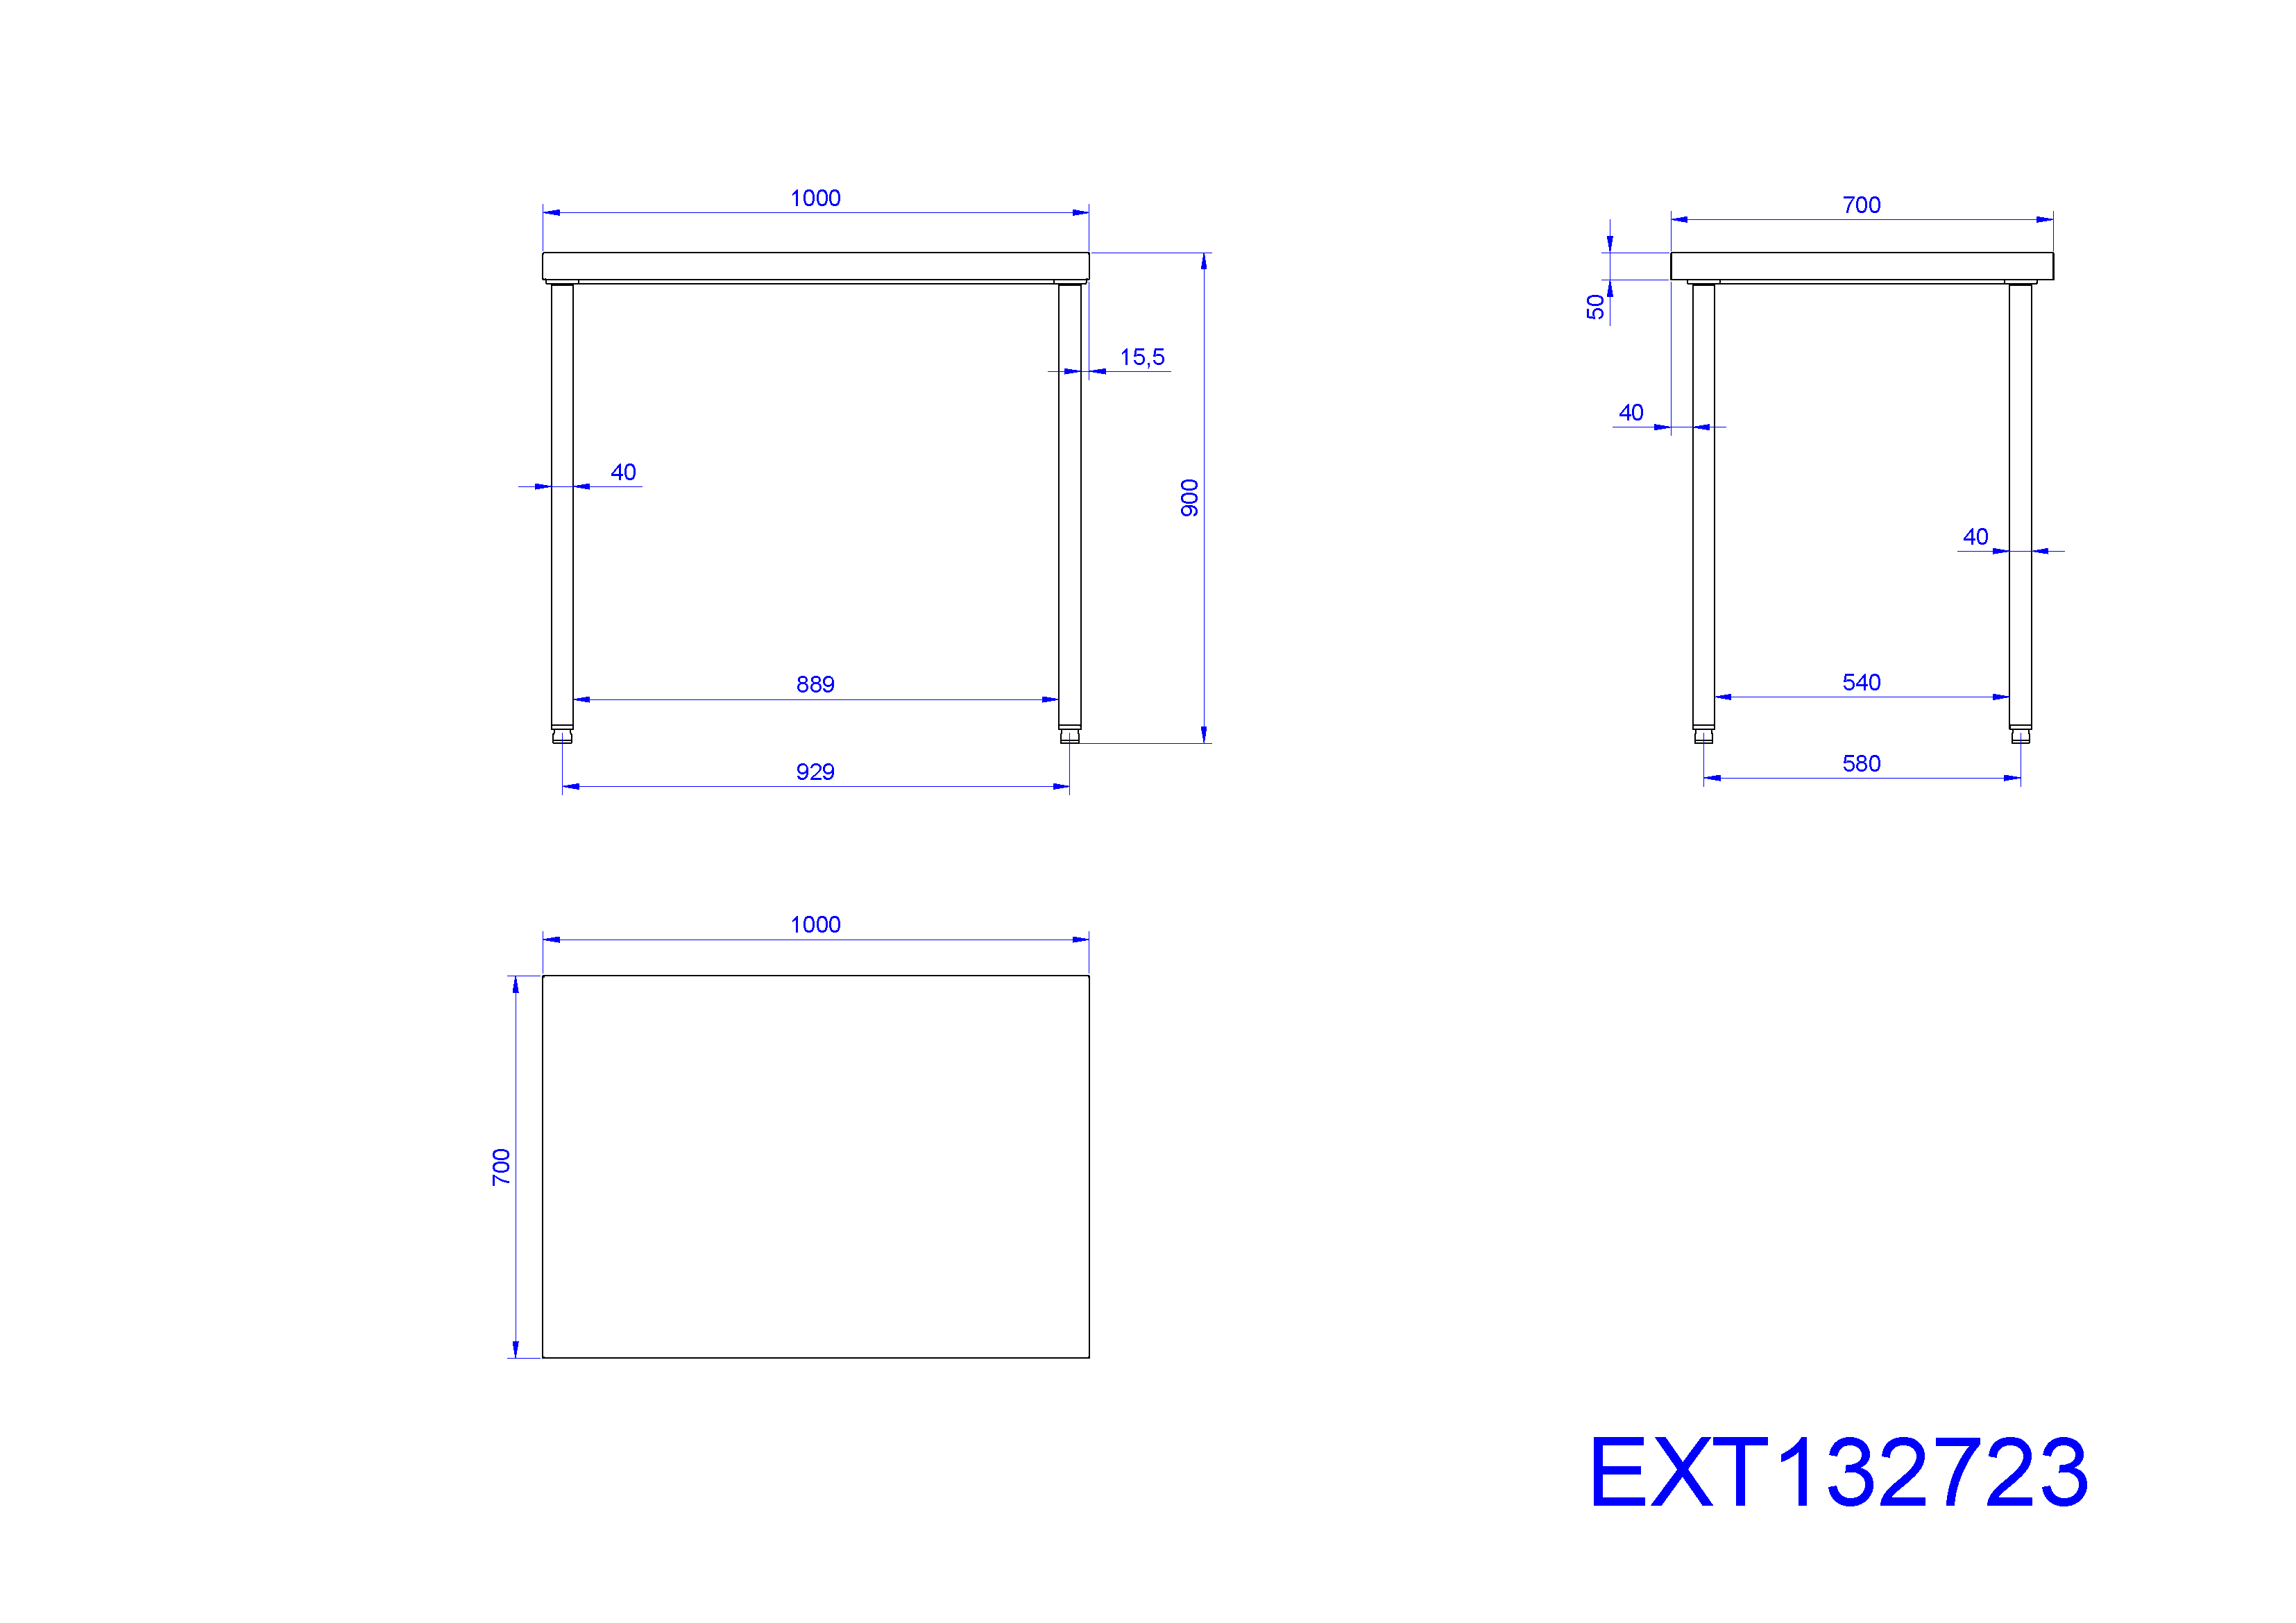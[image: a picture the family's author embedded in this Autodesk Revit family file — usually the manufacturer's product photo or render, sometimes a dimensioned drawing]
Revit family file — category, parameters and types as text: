
# Revit family: QF_ELECTROLUXPROFESSIONAL_133050_TG1400EN
name_source: partatom
category: Attrezzature speciali
units: mm (PartAtom-declared; Revit-internal decimal feet)

## family parameters
Basato su piano di lavoro = No
Condiviso = No
Punto di calcolo locali = No
Quota connettore circolare = Usa diametro
Sempre verticale = Sì
Taglio con vuoti quando caricato = No
Tipo di parte = Normale

## types (1)
- Standard
    Accessory = Sì
    Cold Water Size = 0 mm
    Compressed Air Pressure = 0.0 Pa
    Compressed Air Size = 0 mm
    Compressed Air Volume = 0.0 L/s
    Condensate Return Size = 0 mm
    Cycle = 0 Hz
    Depth Actual = 700 mm  [stored 2.29659 ft]
    Descrizione = WORK TABLE 1400 MM
    Direct Waste Size = 0 mm
    Gas Input Pressure = 0
    Gas KW = 0
    Gas Size = 0 mm
    HP = 0 HP
    Height Actual = 900 mm  [stored 2.95276 ft]
    Hot Water Size = 0 mm
    Item Number = 133050
    Length Actual = 1400 mm  [stored 4.59318 ft]
    Modello = TG1400EN
    Phase = 0
    Produttore = Electrolux Professional
    Prospetto di default = 0 mm  [stored 0 ft]
    Refrigerant Compressor Remote = Sì
    Refrigeration Liquid Line Size = 0 mm  [stored 0 ft]
    Refrigeration Suction Line Size = 0 mm  [stored 0 ft]
    Steam Consumption per Hour = 0
    Steam Supply Maximum Pressure = 0.0 Pa
    Steam Supply Minimum Pressure = 0.0 Pa
    Steam Supply Size = 0 mm
    URL = https://www.electroluxprofessional.com
    URL Manufacturer = https://www.electroluxprofessional.com
    Volts = 0 V
    Watts = 0 W
    Weight = 45.00 kg

note: source unit labels omitted for Gas Input Pressure — the stored unit's dimension contradicts the parameter name (converter mislabeling)

note: [stored X ft] marks values corroborated as IEEE doubles in the binary element streams (Revit-internal decimal feet)

## geometry (parser evidence)
native form markers: Sweep x2
no freeform markers — native parametric forms only
